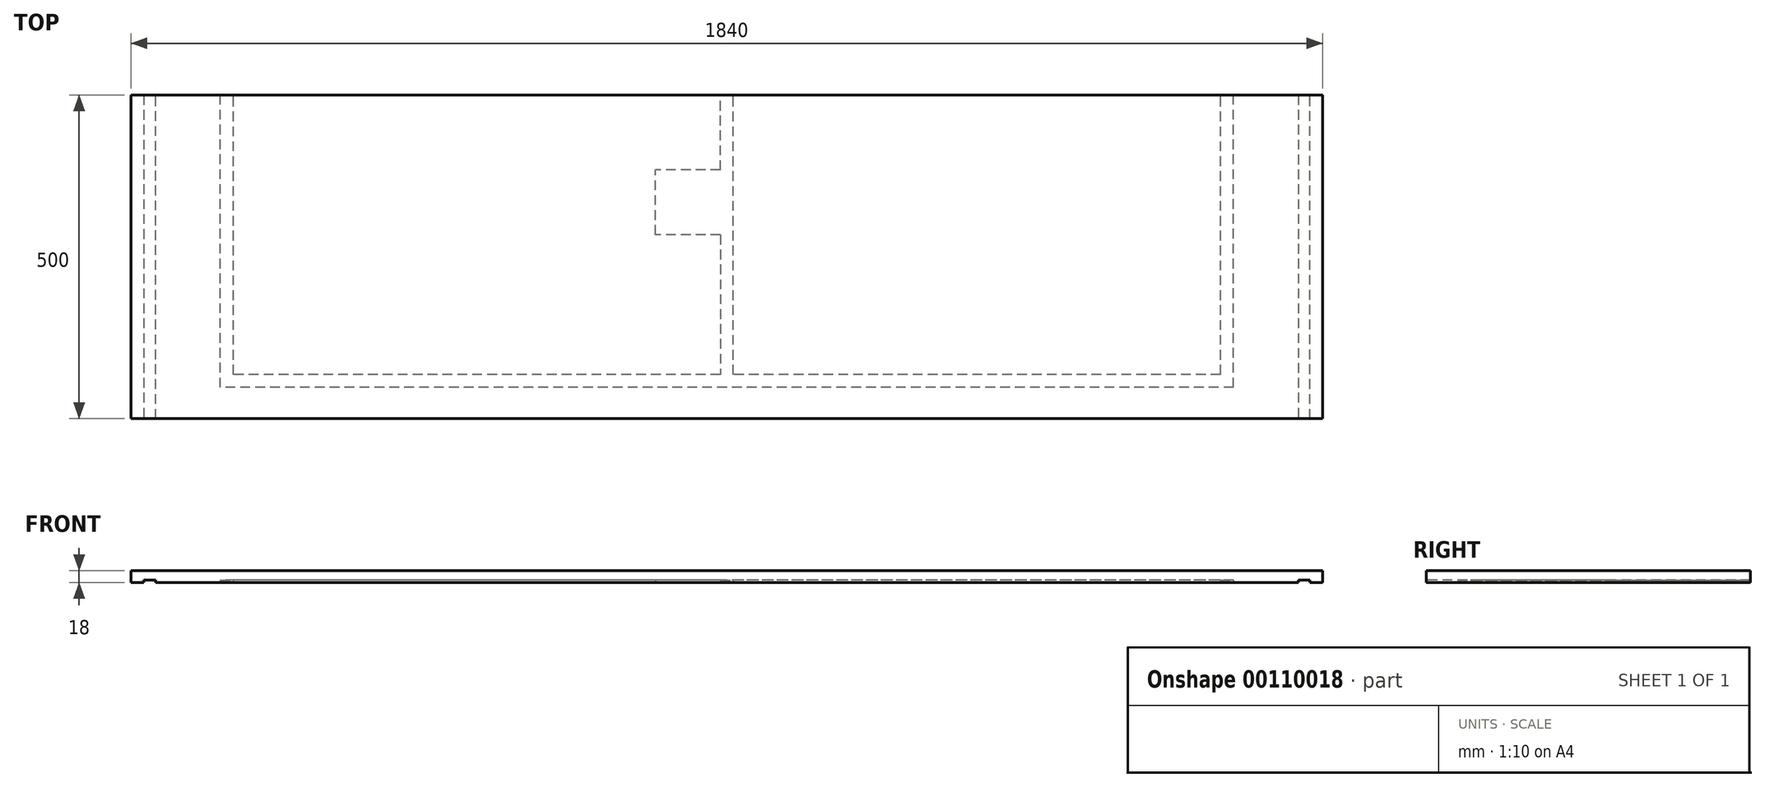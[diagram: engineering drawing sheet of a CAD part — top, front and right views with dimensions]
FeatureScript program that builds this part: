
annotation { "Feature Type Name" : "Feature", "Feature Type Description" : "" }
export const myFeature = defineFeature(function(context is Context, id is Id, definition is map)
    precondition{}
    {
        {
            assignVariable(context, id + "F0", {"name" : "stock_thickness", "anyValue" : 18});
        }
        {
            var Q0;
            Q0=qCreatedBy(makeId("Top.planeOp"),FACE);
            var sketch = newSketch(context, id + "F1", { "sketchPlane" : qUnion([Q0])});
            skLineSegment(sketch, "E0.bottom", {"start": v(0, 0) * mm, "end": v(38, 0) * mm});
            skLineSegment(sketch, "E0.top", {"start": v(0, 500) * mm, "end": v(1840, 500) * mm});
            skLineSegment(sketch, "E0.left", {"start": v(0, 0) * mm, "end": v(0, 500) * mm});
            skLineSegment(sketch, "E0.right", {"start": v(1840, 0) * mm, "end": v(1840, 500) * mm});
            skLineSegment(sketch, "E1", {"start": v(20, 500) * mm, "end": v(20, 0) * mm});
            skLineSegment(sketch, "E2", {"start": v(38, 0) * mm, "end": v(38, 500) * mm});
            skLineSegment(sketch, "E3", {"start": v(1802, 500) * mm, "end": v(1802, 0) * mm});
            skLineSegment(sketch, "E4", {"start": v(1820, 0) * mm, "end": v(1820, 500) * mm});
            skLineSegment(sketch, "E5.top", {"start": v(1682, 68.32) * mm, "end": v(930, 68.32) * mm});
            skLineSegment(sketch, "E5.left", {"start": v(1702, 48.32) * mm, "end": v(1702, 68.32) * mm});
            skLineSegment(sketch, "E5.right", {"start": v(138, 48.32) * mm, "end": v(138, 68.32) * mm});
            skPoint(sketch, "E5.middle", {"position": v(920, 58.32) * mm});
            skLineSegment(sketch, "E6.top", {"start": v(138, 500) * mm, "end": v(158, 500) * mm});
            skLineSegment(sketch, "E6.left", {"start": v(138, 68.32) * mm, "end": v(138, 500) * mm});
            skLineSegment(sketch, "E6.right", {"start": v(158, 68.32) * mm, "end": v(158, 500) * mm});
            skLineSegment(sketch, "E7.top", {"start": v(1702, 500) * mm, "end": v(1682, 500) * mm});
            skLineSegment(sketch, "E7.left", {"start": v(1702, 68.32) * mm, "end": v(1702, 500) * mm});
            skLineSegment(sketch, "E7.right", {"start": v(1682, 68.32) * mm, "end": v(1682, 500) * mm});
            skLineSegment(sketch, "E8.right", {"start": v(910, 284.16) * mm, "end": v(910, 68.32) * mm});
            skLineSegment(sketch, "E9.trimOffspring", {"start": v(910, 68.32) * mm, "end": v(158, 68.32) * mm});
            skLineSegment(sketch, "E10.trimOffspring", {"start": v(1802, 0) * mm, "end": v(1840, 0) * mm});
            skLineSegment(sketch, "E11.right", {"start": v(810, 284.16) * mm, "end": v(810, 384.16) * mm});
            skLineSegment(sketch, "E12.trimOffspring", {"start": v(910, 284.16) * mm, "end": v(810, 284.16) * mm});
            skLineSegment(sketch, "E13", {"start": v(910, 384.16) * mm, "end": v(910, 500) * mm});
            skLineSegment(sketch, "E14.trimOffspring", {"start": v(910, 384.16) * mm, "end": v(810, 384.16) * mm});
            skPoint(sketch, "E15", {"position": v(920, 48.32) * mm});
            skLineSegment(sketch, "E16", {"start": v(930, 68.32) * mm, "end": v(930, 500) * mm});
            skLineSegment(sketch, "E17", {"start": v(920, 48.32) * mm, "end": v(920, 8.03) * mm, "construction": true});
            skLineSegment(sketch, "E18", {"start": v(38, 0) * mm, "end": v(1802, 0) * mm});
            skLineSegment(sketch, "E19", {"start": v(1702, 48.32) * mm, "end": v(138, 48.32) * mm});
            skSolve(sketch);
        }
        {
            var Q0;
            Q0 = qSketchRegion(id + "F1", true);
            extrude(context, id + "F2", {"entities" : qUnion([Q0]), "depth" : (getVariable(context, 'stock_thickness')) * mm});
        }
        {
            var Q0;
            Q0=makeQuery(id+"F1.imprint","IMPRINT",FACE,{"disambiguationData":[TD([[makeQuery(id+"F1.imprint","IMPRINT",EDGE,{"derivedFrom":sQuery(id+"F1.wireOp",EDGE,"E5.top")}),1.0]])]});
            var Q1;
            {var subQ2=sQuery(id+"F1.wireOp",EDGE,"E1");Q1=makeQuery(id+"F1.imprint","IMPRINT",FACE,{"disambiguationData":[TD([[makeQuery(id+"F1.imprint","IMPRINT",EDGE,{"derivedFrom":subQ2}),1.0]])]});}
            var Q2;
            {var subQ0=sQuery(id+"F1.wireOp",EDGE,"E3");Q2=makeQuery(id+"F1.imprint","IMPRINT",FACE,{"disambiguationData":[TD([[makeQuery(id+"F1.imprint","IMPRINT",EDGE,{"derivedFrom":subQ0}),1.0]])]});}
            extrude(context, id + "F3", {"entities" : qUnion([Q0, Q1, Q2]), "operationType" : NewBodyOperationType.REMOVE, "depth" : 4 * mm});
        }
    });
